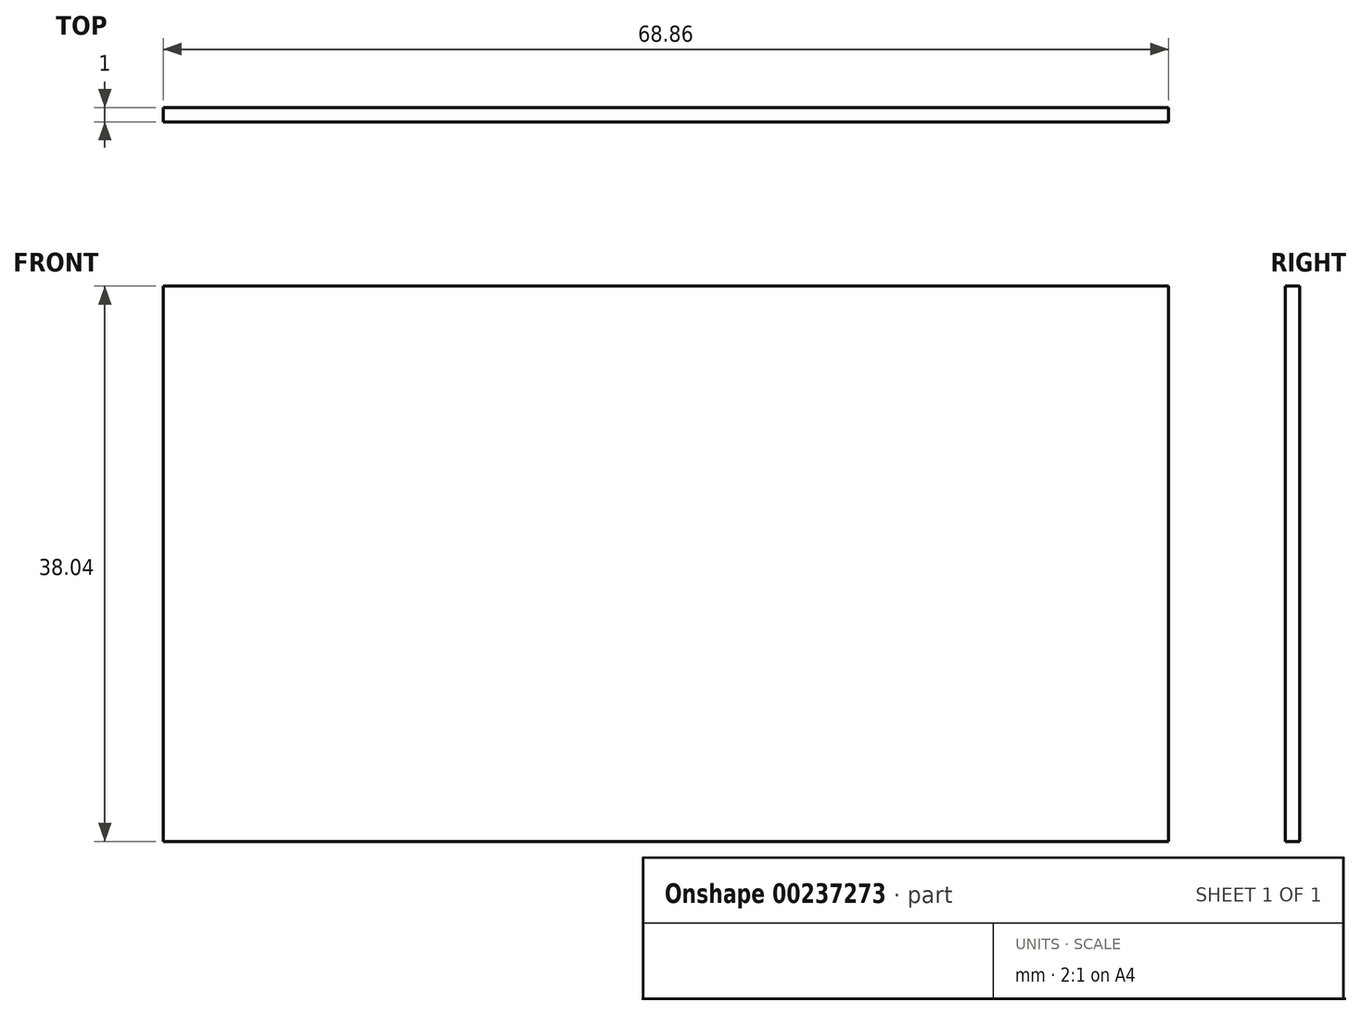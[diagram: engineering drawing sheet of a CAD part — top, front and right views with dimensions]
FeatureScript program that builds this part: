
annotation { "Feature Type Name" : "Feature", "Feature Type Description" : "" }
export const myFeature = defineFeature(function(context is Context, id is Id, definition is map)
    precondition{}
    {
        {
            var Q0;
            Q0=qCreatedBy(makeId("Front.planeOp"),FACE);
            var sketch = newSketch(context, id + "F0", { "sketchPlane" : qUnion([Q0])});
            skLineSegment(sketch, "E0", {"start": v(0, 0) * mm, "end": v(68.86, 0) * mm});
            skLineSegment(sketch, "E1", {"start": v(68.86, 0) * mm, "end": v(68.86, 38.04) * mm});
            skLineSegment(sketch, "E2", {"start": v(68.86, 38.04) * mm, "end": v(0, 38.04) * mm});
            skLineSegment(sketch, "E3", {"start": v(0, 38.04) * mm, "end": v(0, 0) * mm});
            skSolve(sketch);
        }
        {
            var Q0;
            Q0=makeQuery(id+"F0.imprint","IMPRINT",FACE,{"disambiguationData":[TD([[makeQuery(id+"F0.imprint","IMPRINT",EDGE,{"derivedFrom":sQuery(id+"F0.wireOp",EDGE,"E0")}),1.0]])]});
            extrude(context, id + "F1", {"entities" : qUnion([Q0]), "depth" : 1 * mm});
        }
    });
